# Revit family: 56331_3D_ProfiLux-LED-350-01_001
name_source: partatom
category: Körper
revit_build: Autodesk Revit 2015 (Build: 20140606_1530(x64)
units: mm (PartAtom-declared; Revit-internal decimal feet)

## types (1)
- ProfiLux LED 350/01
    Beam angle = 25°  + -2°
    Beschreibung = neutral white light
    Cable length = 4 m
    Colour Rendering Index (CRI) = 80 %
    Colour temerature LED white = 4000 K
    Dim frequency = 2800 Hz
    Dimensions Dxh = 75x70 mm
    Energie efficiency category = A
    Hersteller = OASE GmbH Post Box 2069, 48469 Hörstel , Germany +49 5454 80-0
    Homepage = http://www.oase-livingwater.com
    Luminous flux white = 340 lm
    Material = Stainless steel 1.4404 (AISI 316L)
    Modell = ProfiLux LED 350/01
    Power connection type = 24 V DC plug
    Protection class = 68 IP
    Rated current = 0.31 A
    Rated voltage = 24 V/DC
    Weight = 0.61 kg
    Weighted energy consumption = 8.25 kWh/1000h
    oder no. = 56331
    power consumption = 8 W

## geometry (parser evidence)
native form markers: Blend x6
no freeform markers — native parametric forms only
